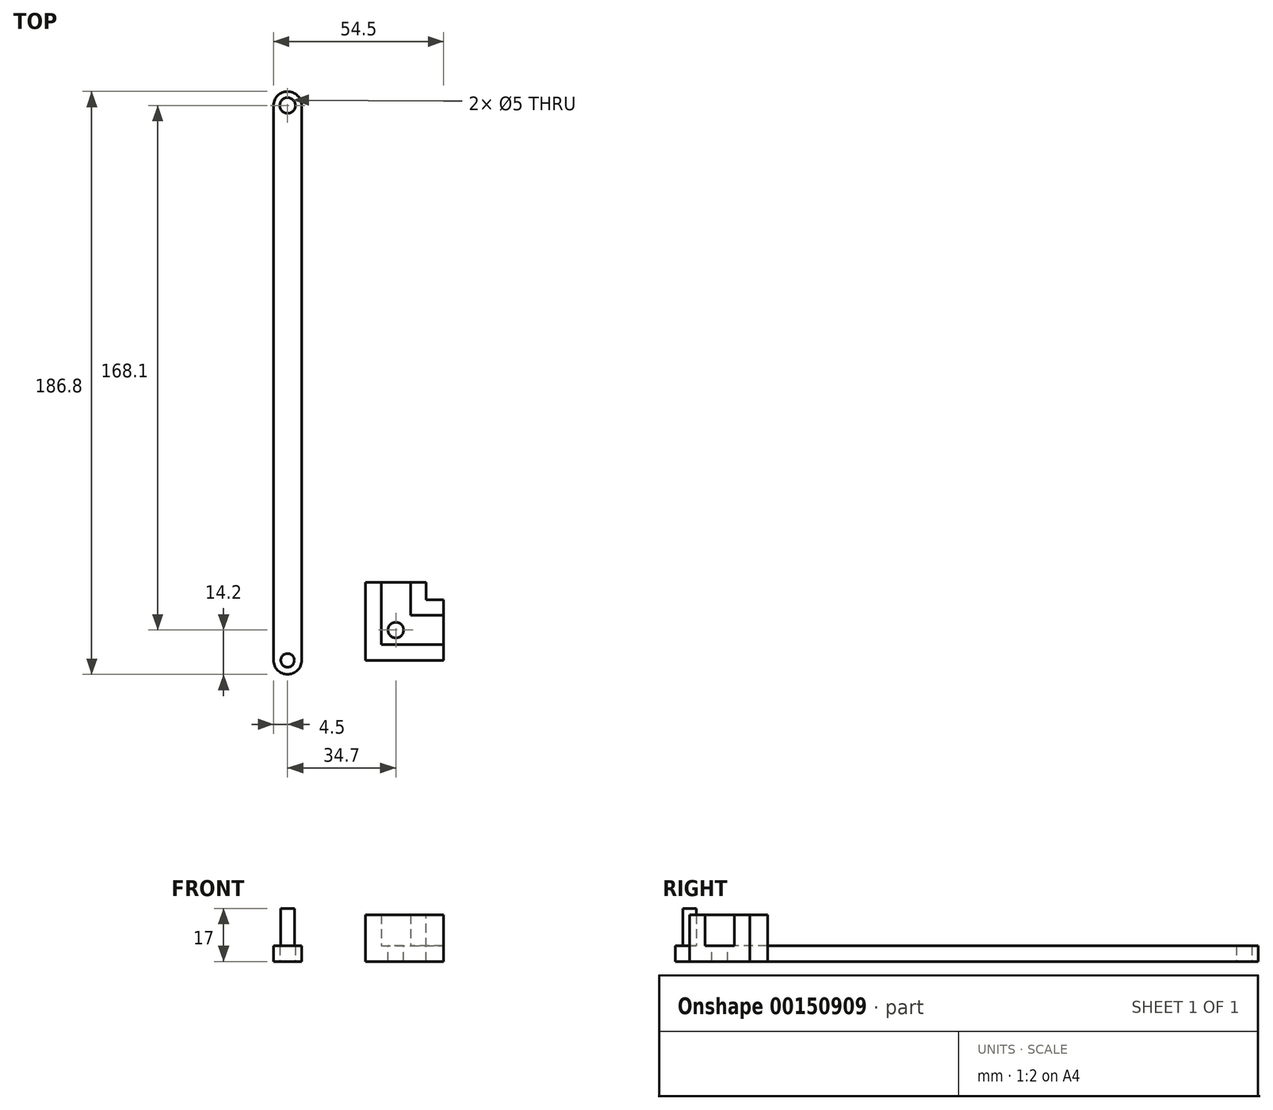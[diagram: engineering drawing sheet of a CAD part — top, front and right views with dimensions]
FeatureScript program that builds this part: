
annotation { "Feature Type Name" : "Feature", "Feature Type Description" : "" }
export const myFeature = defineFeature(function(context is Context, id is Id, definition is map)
    precondition{}
    {
        {
            var Q0;
            Q0=qCreatedBy(makeId("Top.planeOp"),FACE);
            var sketch = newSketch(context, id + "F0", { "sketchPlane" : qUnion([Q0])});
            skLineSegment(sketch, "E0", {"start": v(-4.5, 177.8) * mm, "end": v(-4.5, 0) * mm});
            skLineSegment(sketch, "E1", {"start": v(4.5, 177.8) * mm, "end": v(4.5, 0) * mm});
            skArc(sketch, "E2", {"start": v(4.5, 177.8) * mm, "mid": v(0, 182.3) * mm, "end": v(-4.5, 177.8) * mm});
            skArc(sketch, "E3", {"start": v(-4.5, 0) * mm, "mid": v(0, -4.5) * mm, "end": v(4.5, 0) * mm});
            skCircle(sketch, "E4", {"center": v(0, 177.8) * mm, "radius": 2.5 * mm});
            skSolve(sketch);
        }
        {
            var Q0;
            Q0 = qSketchRegion(id + "F0", true);
            extrude(context, id + "F1", {"entities" : qUnion([Q0]), "depth" : 5 * mm});
        }
        {
            var Q0;
            Q0=makeQuery(id+"F1.opExtrude","CAP_FACE",FACE,{"disambiguationData":[OSD([sQuery(id+"F0.wireOp",EDGE,"E0"),sQuery(id+"F0.wireOp",EDGE,"E1"),sQuery(id+"F0.wireOp",EDGE,"E2"),sQuery(id+"F0.wireOp",EDGE,"E3"),sQuery(id+"F0.wireOp",EDGE,"E4")])],"isStart":false});
            var sketch = newSketch(context, id + "F2", { "sketchPlane" : qUnion([Q0])});
            skCircle(sketch, "E5", {"center": v(0, 0) * mm, "radius": 2.18 * mm});
            skSolve(sketch);
        }
        {
            var Q0;
            Q0 = qSketchRegion(id + "F2", true);
            extrude(context, id + "F3", {"entities" : qUnion([Q0]), "operationType" : NewBodyOperationType.ADD, "depth" : 12 * mm});
        }
        {
            var Q0;
            Q0=qCreatedBy(makeId("Top.planeOp"),FACE);
            var sketch = newSketch(context, id + "F4", { "sketchPlane" : qUnion([Q0])});
            skLineSegment(sketch, "E6.bottom", {"start": v(25, 25) * mm, "end": v(50, 25) * mm});
            skLineSegment(sketch, "E6.top", {"start": v(25, 0) * mm, "end": v(50, 0) * mm});
            skLineSegment(sketch, "E6.left", {"start": v(25, 25) * mm, "end": v(25, 0) * mm});
            skLineSegment(sketch, "E6.right", {"start": v(50, 25) * mm, "end": v(50, 0) * mm});
            skSolve(sketch);
        }
        {
            var Q0;
            Q0 = qSketchRegion(id + "F4", true);
            extrude(context, id + "F5", {"entities" : qUnion([Q0]), "depth" : 5 * mm});
        }
        {
            var Q0;
            Q0=makeQuery(id+"F5.opExtrude","CAP_FACE",FACE,{"disambiguationData":[OSD([sQuery(id+"F4.wireOp",EDGE,"E6.bottom"),sQuery(id+"F4.wireOp",EDGE,"E6.top"),sQuery(id+"F4.wireOp",EDGE,"E6.left"),sQuery(id+"F4.wireOp",EDGE,"E6.right")])],"isStart":false});
            var sketch = newSketch(context, id + "F6", { "sketchPlane" : qUnion([Q0])});
            skLineSegment(sketch, "E7.bottom", {"start": v(25, 25) * mm, "end": v(30, 25) * mm});
            skLineSegment(sketch, "E7.right", {"start": v(30, 25) * mm, "end": v(30, 5) * mm});
            skLineSegment(sketch, "E8.top", {"start": v(30, 5) * mm, "end": v(50, 5) * mm});
            skLineSegment(sketch, "E8.right", {"start": v(50, 0) * mm, "end": v(50, 5) * mm});
            skLineSegment(sketch, "E9.bottom", {"start": v(50, 25) * mm, "end": v(39.4, 25) * mm});
            skLineSegment(sketch, "E9.top", {"start": v(50, 14.4) * mm, "end": v(39.4, 14.4) * mm});
            skLineSegment(sketch, "E9.left", {"start": v(50, 25) * mm, "end": v(50, 14.4) * mm});
            skLineSegment(sketch, "E9.right", {"start": v(39.4, 25) * mm, "end": v(39.4, 14.4) * mm});
            skLineSegment(sketch, "E10", {"start": v(25, 25) * mm, "end": v(25, 0) * mm});
            skLineSegment(sketch, "E11", {"start": v(25, 0) * mm, "end": v(50, 0) * mm});
            skSolve(sketch);
        }
        {
            var Q0;
            Q0 = qSketchRegion(id + "F6", true);
            extrude(context, id + "F7", {"entities" : qUnion([Q0]), "operationType" : NewBodyOperationType.ADD, "depth" : 10 * mm});
        }
        {
            var Q0;
            Q0=makeQuery(id+"F5.opExtrude","CAP_FACE",FACE,{"disambiguationData":[OSD([sQuery(id+"F4.wireOp",EDGE,"E6.bottom"),sQuery(id+"F4.wireOp",EDGE,"E6.top"),sQuery(id+"F4.wireOp",EDGE,"E6.left"),sQuery(id+"F4.wireOp",EDGE,"E6.right")])],"isStart":false});
            var sketch = newSketch(context, id + "F8", { "sketchPlane" : qUnion([Q0])});
            skCircle(sketch, "E12", {"center": v(34.7, 9.7) * mm, "radius": 2.5 * mm});
            skLineSegment(sketch, "E13", {"start": v(39.4, 14.4) * mm, "end": v(30, 5) * mm, "construction": true});
            skSolve(sketch);
        }
        {
            var Q0;
            Q0 = qSketchRegion(id + "F8", true);
            extrude(context, id + "F9", {"entities" : qUnion([Q0]), "operationType" : NewBodyOperationType.REMOVE, "oppositeDirection" : true, "depth" : 25 * mm});
        }
        {
            var Q0;
            Q0=makeQuery(id+"F7.opExtrude","CAP_FACE",FACE,{"disambiguationData":[OSD([sQuery(id+"F6.wireOp",EDGE,"E9.bottom"),sQuery(id+"F6.wireOp",EDGE,"E9.top"),sQuery(id+"F6.wireOp",EDGE,"E9.left"),sQuery(id+"F6.wireOp",EDGE,"E9.right")])],"isStart":false});
            var sketch = newSketch(context, id + "F10", { "sketchPlane" : qUnion([Q0])});
            skLineSegment(sketch, "E14.bottom", {"start": v(50, 25) * mm, "end": v(44.4, 25) * mm});
            skLineSegment(sketch, "E14.top", {"start": v(50, 19.4) * mm, "end": v(44.4, 19.4) * mm});
            skLineSegment(sketch, "E14.left", {"start": v(50, 25) * mm, "end": v(50, 19.4) * mm});
            skLineSegment(sketch, "E14.right", {"start": v(44.4, 25) * mm, "end": v(44.4, 19.4) * mm});
            skSolve(sketch);
        }
        {
            var Q0;
            Q0 = qSketchRegion(id + "F10", true);
            extrude(context, id + "F11", {"entities" : qUnion([Q0]), "operationType" : NewBodyOperationType.REMOVE, "oppositeDirection" : true, "depth" : 25 * mm});
        }
    });
